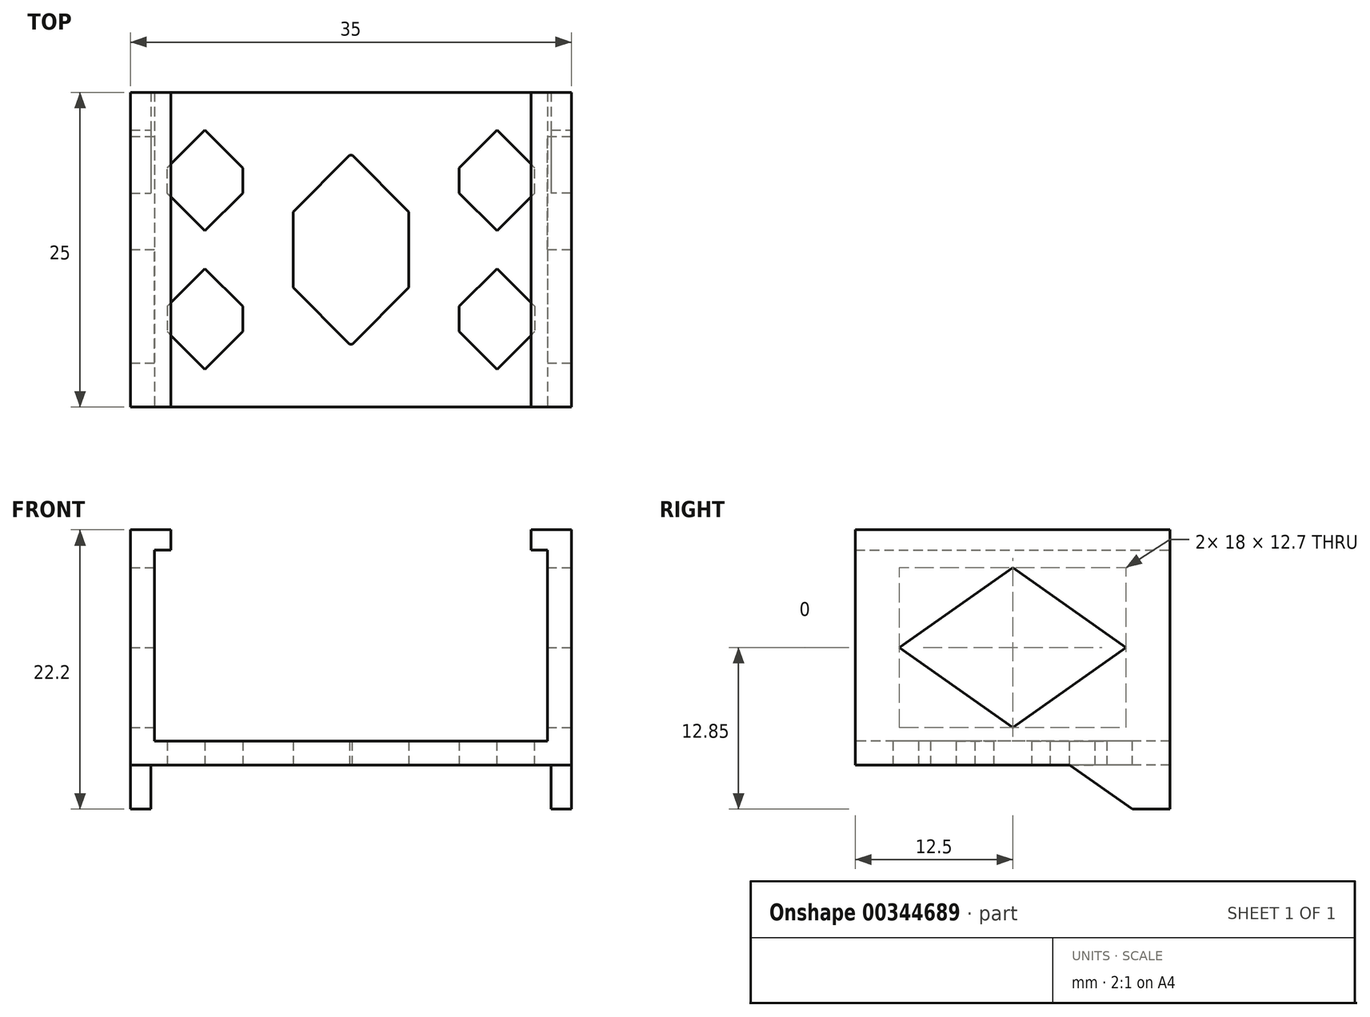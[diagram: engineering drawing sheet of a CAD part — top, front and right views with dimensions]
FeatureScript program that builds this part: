
annotation { "Feature Type Name" : "Feature", "Feature Type Description" : "" }
export const myFeature = defineFeature(function(context is Context, id is Id, definition is map)
    precondition{}
    {
        {
            var Q0;
            Q0=qCreatedBy(makeId("Top.planeOp"),FACE);
            var sketch = newSketch(context, id + "F0", { "sketchPlane" : qUnion([Q0])});
            skLineSegment(sketch, "E0.bottom", {"start": v(-17.5, 15) * mm, "end": v(17.5, 15) * mm});
            skLineSegment(sketch, "E0.top", {"start": v(-17.5, -15) * mm, "end": v(17.5, -15) * mm});
            skLineSegment(sketch, "E0.left", {"start": v(-17.5, 15) * mm, "end": v(-17.5, -15) * mm});
            skLineSegment(sketch, "E0.right", {"start": v(17.5, 15) * mm, "end": v(17.5, -15) * mm});
            skPoint(sketch, "E0.middle", {"position": v(0, 0) * mm});
            skSolve(sketch);
        }
        {
            var Q0;
            Q0=makeQuery(id+"F0.imprint","IMPRINT",FACE,{"disambiguationData":[TD([[makeQuery(id+"F0.imprint","IMPRINT",EDGE,{"derivedFrom":sQuery(id+"F0.wireOp",EDGE,"E0.bottom")}),-1.0]])]});
            extrude(context, id + "F1", {"entities" : qUnion([Q0]), "depth" : 1.9 * mm});
        }
        {
            var Q0;
            {var subQ5=sQuery(id+"F0.wireOp",EDGE,"E0.right");var subQ6=sQuery(id+"F0.wireOp",EDGE,"E0.left");var subQ7=sQuery(id+"F0.wireOp",EDGE,"E0.top");var subQ8=sQuery(id+"F0.wireOp",EDGE,"E0.bottom");var subQ9=makeQuery(id+"F1.opExtrude","CAP_FACE",FACE,{"disambiguationData":[OSD([subQ8,subQ7,subQ6,subQ5])],"isStart":false});var subQ12=subQ9;Q0=makeQuery(id+"FTskU3KK5imesQs_1.opFillet","MERGE",FACE,{"derivedFrom":[makeQuery(id+"FZi3CJKkktuihJ1_1.boolean.opBoolean","SPLIT",FACE,{"disambiguationData":[TD([makeQuery(id+"F1.opExtrude","SWEPT_FACE",FACE,{"disambiguationData":[OSD([subQ8])]})])],"derivedFrom":subQ12}),makeQuery(id+"FZ7EBSF1tdb4njM_1.boolean.opBoolean","MERGE",FACE,{"derivedFrom":[makeQuery(id+"FZi3CJKkktuihJ1_1.boolean.opBoolean","SPLIT",FACE,{"disambiguationData":[TD([makeQuery(id+"FlsG0jWeIkAughT_1.opExtrude","SWEPT_FACE",FACE,{"disambiguationData":[OSD([sQuery(id+"F5Wyuop6bpOGen8_1.wireOp",EDGE,"vaNtV44L-idVL-UOBQ-HHhe-vYpkaX2QMto8.bottom")])]})])],"derivedFrom":subQ12}),makeQuery(id+"FZ7EBSF1tdb4njM_1.opExtrude","CAP_FACE",FACE,{"disambiguationData":[OSD([sQuery(id+"FoSm93bD1NxVTFu_1.wireOp",EDGE,"97a7e462-43fe-4127-a601-1d90c2ab95a00.MirrorCS"),sQuery(id+"FoSm93bD1NxVTFu_1.wireOp",EDGE,"97a7e462-43fe-4127-a601-1d90c2ab95a01.MirrorCS"),sQuery(id+"FoSm93bD1NxVTFu_1.wireOp",EDGE,"97a7e462-43fe-4127-a601-1d90c2ab95a02.MirrorCS"),sQuery(id+"FoSm93bD1NxVTFu_1.wireOp",EDGE,"97a7e462-43fe-4127-a601-1d90c2ab95a03.MirrorCS")])],"isStart":false})]}),makeQuery(id+"FZ7EBSF1tdb4njM_1.boolean.opBoolean","MERGE",FACE,{"derivedFrom":[makeQuery(id+"FZi3CJKkktuihJ1_1.boolean.opBoolean","SPLIT",FACE,{"disambiguationData":[TD([makeQuery(id+"FlsG0jWeIkAughT_1.opExtrude","SWEPT_FACE",FACE,{"disambiguationData":[OSD([sQuery(id+"F5Wyuop6bpOGen8_1.wireOp",EDGE,"5b2c8ccd-c1e1-48dd-aecc-73c440124aab0.MirrorCS")])]})])],"derivedFrom":subQ12}),makeQuery(id+"FZ7EBSF1tdb4njM_1.opExtrude","CAP_FACE",FACE,{"disambiguationData":[OSD([sQuery(id+"FoSm93bD1NxVTFu_1.wireOp",EDGE,"85c03d27-702a-4580-8be8-e1d3315b53173.MirrorCS"),sQuery(id+"FoSm93bD1NxVTFu_1.wireOp",EDGE,"85c03d27-702a-4580-8be8-e1d3315b53174.MirrorCS"),sQuery(id+"FoSm93bD1NxVTFu_1.wireOp",EDGE,"85c03d27-702a-4580-8be8-e1d3315b53176.MirrorCS"),sQuery(id+"FoSm93bD1NxVTFu_1.wireOp",EDGE,"85c03d27-702a-4580-8be8-e1d3315b53177.MirrorCS")])],"isStart":false})]})]});}
            var sketch = newSketch(context, id + "F2", { "sketchPlane" : qUnion([Q0])});
            skLineSegment(sketch, "E1.bottom", {"start": v(-15.6, 14) * mm, "end": v(15.6, 14) * mm});
            skLineSegment(sketch, "E1.top", {"start": v(-15.6, -14) * mm, "end": v(15.6, -14) * mm});
            skLineSegment(sketch, "E1.left", {"start": v(-15.6, 14) * mm, "end": v(-15.6, -14) * mm});
            skLineSegment(sketch, "E1.right", {"start": v(15.6, 14) * mm, "end": v(15.6, -14) * mm});
            skPoint(sketch, "E1.middle", {"position": v(0, 0) * mm});
            skSolve(sketch);
        }
        {
            var Q0;
            Q0=makeQuery(id+"F2.imprint","IMPRINT",FACE,{"disambiguationData":[TD([[makeQuery(id+"F2.imprint","IMPRINT",EDGE,{"derivedFrom":sQuery(id+"F2.wireOp",EDGE,"E1.bottom")}),1.0]])]});
            extrude(context, id + "F3", {"entities" : qUnion([Q0]), "operationType" : NewBodyOperationType.ADD, "depth" : 16.8 * mm});
        }
        {
            var Q0;
            Q0=makeQuery(id+"F3.opExtrude","CAP_FACE",FACE,{"disambiguationData":[OSD([sQuery(id+"F0.wireOp",EDGE,"E0.bottom"),sQuery(id+"F0.wireOp",EDGE,"E0.top"),sQuery(id+"F0.wireOp",EDGE,"E0.left"),sQuery(id+"F0.wireOp",EDGE,"E0.right"),sQuery(id+"F2.wireOp",EDGE,"E1.bottom"),sQuery(id+"F2.wireOp",EDGE,"E1.top"),sQuery(id+"F2.wireOp",EDGE,"E1.left"),sQuery(id+"F2.wireOp",EDGE,"E1.right")])],"isStart":false});
            var sketch = newSketch(context, id + "F4", { "sketchPlane" : qUnion([Q0])});
            skLineSegment(sketch, "E2.bottom", {"start": v(-17.5, -15) * mm, "end": v(17.5, -15) * mm});
            skLineSegment(sketch, "E2.top", {"start": v(-17.5, -12.5) * mm, "end": v(17.5, -12.5) * mm});
            skLineSegment(sketch, "E2.left", {"start": v(-17.5, -15) * mm, "end": v(-17.5, -12.5) * mm});
            skLineSegment(sketch, "E2.right", {"start": v(17.5, -15) * mm, "end": v(17.5, -12.5) * mm});
            skLineSegment(sketch, "E3.MirrorCS", {"start": v(17.5, 15) * mm, "end": v(17.5, 12.5) * mm});
            skLineSegment(sketch, "E4.MirrorCS", {"start": v(-17.5, 15) * mm, "end": v(-17.5, 12.5) * mm});
            skLineSegment(sketch, "E5.MirrorCS", {"start": v(-17.5, 15) * mm, "end": v(17.5, 15) * mm});
            skLineSegment(sketch, "E6.MirrorCS", {"start": v(-17.5, 12.5) * mm, "end": v(17.5, 12.5) * mm});
            skSolve(sketch);
        }
        {
            var Q0;
            Q0=qSketchRegion(id+"F4",true);
            extrude(context, id + "F5", {"entities" : qUnion([Q0]), "operationType" : NewBodyOperationType.REMOVE, "endBound" : BoundingType.THROUGH_ALL, "oppositeDirection" : true, "depth" : 25 * mm});
        }
        {
            var Q0;
            {var subQ5=sQuery(id+"F0.wireOp",EDGE,"E0.right");var subQ6=sQuery(id+"F0.wireOp",EDGE,"E0.left");var subQ7=sQuery(id+"F0.wireOp",EDGE,"E0.top");var subQ8=sQuery(id+"F0.wireOp",EDGE,"E0.bottom");var subQ9=makeQuery(id+"F1.opExtrude","CAP_FACE",FACE,{"disambiguationData":[OSD([subQ8,subQ7,subQ6,subQ5])],"isStart":false});var subQ12=subQ9;Q0=makeQuery(id+"FTskU3KK5imesQs_1.opFillet","MERGE",FACE,{"derivedFrom":[makeQuery(id+"FZi3CJKkktuihJ1_1.boolean.opBoolean","SPLIT",FACE,{"disambiguationData":[TD([makeQuery(id+"F1.opExtrude","SWEPT_FACE",FACE,{"disambiguationData":[OSD([subQ8])]})])],"derivedFrom":subQ12}),makeQuery(id+"FZ7EBSF1tdb4njM_1.boolean.opBoolean","MERGE",FACE,{"derivedFrom":[makeQuery(id+"FZi3CJKkktuihJ1_1.boolean.opBoolean","SPLIT",FACE,{"disambiguationData":[TD([makeQuery(id+"FlsG0jWeIkAughT_1.opExtrude","SWEPT_FACE",FACE,{"disambiguationData":[OSD([sQuery(id+"F5Wyuop6bpOGen8_1.wireOp",EDGE,"vaNtV44L-idVL-UOBQ-HHhe-vYpkaX2QMto8.bottom")])]})])],"derivedFrom":subQ12}),makeQuery(id+"FZ7EBSF1tdb4njM_1.opExtrude","CAP_FACE",FACE,{"disambiguationData":[OSD([sQuery(id+"FoSm93bD1NxVTFu_1.wireOp",EDGE,"97a7e462-43fe-4127-a601-1d90c2ab95a00.MirrorCS"),sQuery(id+"FoSm93bD1NxVTFu_1.wireOp",EDGE,"97a7e462-43fe-4127-a601-1d90c2ab95a01.MirrorCS"),sQuery(id+"FoSm93bD1NxVTFu_1.wireOp",EDGE,"97a7e462-43fe-4127-a601-1d90c2ab95a02.MirrorCS"),sQuery(id+"FoSm93bD1NxVTFu_1.wireOp",EDGE,"97a7e462-43fe-4127-a601-1d90c2ab95a03.MirrorCS")])],"isStart":false})]}),makeQuery(id+"FZ7EBSF1tdb4njM_1.boolean.opBoolean","MERGE",FACE,{"derivedFrom":[makeQuery(id+"FZi3CJKkktuihJ1_1.boolean.opBoolean","SPLIT",FACE,{"disambiguationData":[TD([makeQuery(id+"FlsG0jWeIkAughT_1.opExtrude","SWEPT_FACE",FACE,{"disambiguationData":[OSD([sQuery(id+"F5Wyuop6bpOGen8_1.wireOp",EDGE,"5b2c8ccd-c1e1-48dd-aecc-73c440124aab0.MirrorCS")])]})])],"derivedFrom":subQ12}),makeQuery(id+"FZ7EBSF1tdb4njM_1.opExtrude","CAP_FACE",FACE,{"disambiguationData":[OSD([sQuery(id+"FoSm93bD1NxVTFu_1.wireOp",EDGE,"85c03d27-702a-4580-8be8-e1d3315b53173.MirrorCS"),sQuery(id+"FoSm93bD1NxVTFu_1.wireOp",EDGE,"85c03d27-702a-4580-8be8-e1d3315b53174.MirrorCS"),sQuery(id+"FoSm93bD1NxVTFu_1.wireOp",EDGE,"85c03d27-702a-4580-8be8-e1d3315b53176.MirrorCS"),sQuery(id+"FoSm93bD1NxVTFu_1.wireOp",EDGE,"85c03d27-702a-4580-8be8-e1d3315b53177.MirrorCS")])],"isStart":false})]})]});}
            var sketch = newSketch(context, id + "F6", { "sketchPlane" : qUnion([Q0])});
            skLineSegment(sketch, "E7.bottom", {"start": v(-15.6, -5.25) * mm, "end": v(-13.6, -5.25) * mm});
            skLineSegment(sketch, "E7.top", {"start": v(-15.6, 5.25) * mm, "end": v(-13.6, 5.25) * mm});
            skLineSegment(sketch, "E7.left", {"start": v(-15.6, -5.25) * mm, "end": v(-15.6, 5.25) * mm});
            skLineSegment(sketch, "E7.right", {"start": v(15.6, -5.25) * mm, "end": v(15.6, 5.25) * mm});
            skLineSegment(sketch, "E8.bottom", {"start": v(-15.6, -7.25) * mm, "end": v(-13.6, -7.25) * mm});
            skLineSegment(sketch, "E8.top", {"start": v(-15.6, -12.5) * mm, "end": v(-13.6, -12.5) * mm});
            skLineSegment(sketch, "E8.left", {"start": v(-15.6, -7.25) * mm, "end": v(-15.6, -12.5) * mm});
            skLineSegment(sketch, "E8.right", {"start": v(15.6, -7.25) * mm, "end": v(15.6, -12.5) * mm});
            skLineSegment(sketch, "E9.MirrorCS", {"start": v(-15.6, 7.25) * mm, "end": v(-13.6, 7.25) * mm});
            skLineSegment(sketch, "E10.MirrorCS", {"start": v(-15.6, 12.5) * mm, "end": v(15.6, 12.5) * mm});
            skLineSegment(sketch, "E11.MirrorCS", {"start": v(15.6, 7.25) * mm, "end": v(15.6, 12.5) * mm});
            skLineSegment(sketch, "E12.MirrorCS", {"start": v(-15.6, 7.25) * mm, "end": v(-15.6, 12.5) * mm});
            skLineSegment(sketch, "E13", {"start": v(-13.6, -12.5) * mm, "end": v(-13.6, -7.25) * mm});
            skLineSegment(sketch, "E14.MirrorCS", {"start": v(13.6, -12.5) * mm, "end": v(13.6, -7.25) * mm});
            skLineSegment(sketch, "E15.trimOffspring", {"start": v(-13.6, -5.25) * mm, "end": v(-13.6, 5.25) * mm});
            skLineSegment(sketch, "E16.trimOffspring", {"start": v(13.6, -7.25) * mm, "end": v(15.6, -7.25) * mm});
            skLineSegment(sketch, "E17.trimOffspring", {"start": v(13.6, -12.5) * mm, "end": v(15.6, -12.5) * mm});
            skLineSegment(sketch, "E18.trimOffspring", {"start": v(13.6, -5.25) * mm, "end": v(15.6, -5.25) * mm});
            skLineSegment(sketch, "E19.trimOffspring", {"start": v(13.6, 5.25) * mm, "end": v(15.6, 5.25) * mm});
            skLineSegment(sketch, "E20.trimOffspring", {"start": v(13.6, 7.25) * mm, "end": v(15.6, 7.25) * mm});
            skLineSegment(sketch, "E21.trimOffspring", {"start": v(-13.6, 7.25) * mm, "end": v(-13.6, 12.5) * mm});
            skLineSegment(sketch, "E22.trimOffspring", {"start": v(13.6, -5.25) * mm, "end": v(13.6, 5.25) * mm});
            skLineSegment(sketch, "E23.trimOffspring", {"start": v(13.6, 7.25) * mm, "end": v(13.6, 12.5) * mm});
            skSolve(sketch);
        }
        {
            var Q0;
            Q0=makeQuery(id+"F6.imprint","IMPRINT",FACE,{"disambiguationData":[TD([[makeQuery(id+"F6.imprint","IMPRINT",EDGE,{"derivedFrom":sQuery(id+"F6.wireOp",EDGE,"E8.bottom")}),-1.0]])]});
            var Q1;
            Q1=makeQuery(id+"F6.imprint","IMPRINT",FACE,{"disambiguationData":[TD([[makeQuery(id+"F6.imprint","IMPRINT",EDGE,{"derivedFrom":sQuery(id+"F6.wireOp",EDGE,"E7.bottom")}),1.0]])]});
            var Q2;
            Q2=makeQuery(id+"F6.imprint","IMPRINT",FACE,{"disambiguationData":[TD([[makeQuery(id+"F6.imprint","IMPRINT",EDGE,{"derivedFrom":sQuery(id+"F6.wireOp",EDGE,"E9.MirrorCS")}),1.0]])]});
            var Q3;
            Q3=makeQuery(id+"F6.imprint","IMPRINT",FACE,{"disambiguationData":[TD([[makeQuery(id+"F6.imprint","IMPRINT",EDGE,{"derivedFrom":sQuery(id+"F6.wireOp",EDGE,"E8.right")}),-1.0]])]});
            var Q4;
            Q4=makeQuery(id+"F6.imprint","IMPRINT",FACE,{"disambiguationData":[TD([[makeQuery(id+"F6.imprint","IMPRINT",EDGE,{"derivedFrom":sQuery(id+"F6.wireOp",EDGE,"E7.right")}),-1.0]])]});
            var Q5;
            {var subQ0=sQuery(id+"F6.wireOp",EDGE,"E11.MirrorCS");Q5=makeQuery(id+"F6.imprint","IMPRINT",FACE,{"disambiguationData":[TD([[makeQuery(id+"F6.imprint","IMPRINT",EDGE,{"derivedFrom":subQ0}),-1.0]])]});}
            extrude(context, id + "F7", {"entities" : qUnion([Q0, Q1, Q2, Q3, Q4, Q5]), "operationType" : NewBodyOperationType.REMOVE, "depth" : 30 * mm});
        }
        {
            var Q0;
            Q0=makeQuery(id+"F5.boolean.opBoolean","COPY",FACE,{"derivedFrom":makeQuery(id+"F5.opExtrude","SWEPT_FACE",FACE,{"disambiguationData":[OSD([sQuery(id+"F4.wireOp",EDGE,"E6.MirrorCS")])]})});
            var sketch = newSketch(context, id + "F8", { "sketchPlane" : qUnion([Q0])});
            skLineSegment(sketch, "E24", {"start": v(-15.6, 18.7) * mm, "end": v(-14.3, 18.7) * mm});
            skLineSegment(sketch, "E25", {"start": v(-15.6, 17.1) * mm, "end": v(-15.6, 18.7) * mm});
            skLineSegment(sketch, "E26", {"start": v(-15.6, 17.1) * mm, "end": v(-14.3, 17.1) * mm});
            skLineSegment(sketch, "E27", {"start": v(-14.3, 17.1) * mm, "end": v(-14.3, 18.7) * mm});
            skLineSegment(sketch, "E28.MirrorCS", {"start": v(15.6, 18.7) * mm, "end": v(14.3, 18.7) * mm});
            skLineSegment(sketch, "E29.MirrorCS", {"start": v(15.6, 17.1) * mm, "end": v(14.3, 17.1) * mm});
            skLineSegment(sketch, "E30.MirrorCS", {"start": v(15.6, 17.1) * mm, "end": v(15.6, 18.7) * mm});
            skLineSegment(sketch, "E31.MirrorCS", {"start": v(14.3, 17.1) * mm, "end": v(14.3, 18.7) * mm});
            skSolve(sketch);
        }
        {
            var Q0;
            Q0=makeQuery(id+"F8.imprint","IMPRINT",FACE,{"disambiguationData":[TD([[makeQuery(id+"F8.imprint","IMPRINT",EDGE,{"derivedFrom":sQuery(id+"F8.wireOp",EDGE,"E24")}),-1.0]])]});
            var Q1;
            Q1=makeQuery(id+"F8.imprint","IMPRINT",FACE,{"disambiguationData":[TD([[makeQuery(id+"F8.imprint","IMPRINT",EDGE,{"derivedFrom":sQuery(id+"F8.wireOp",EDGE,"E28.MirrorCS")}),1.0]])]});
            var Q2;
            Q2=makeQuery(id+"F5.boolean.opBoolean","COPY",FACE,{"derivedFrom":makeQuery(id+"F5.opExtrude","SWEPT_FACE",FACE,{"disambiguationData":[OSD([sQuery(id+"F4.wireOp",EDGE,"E2.top")])]})});
            extrude(context, id + "F9", {"entities" : qUnion([Q0, Q1]), "operationType" : NewBodyOperationType.ADD, "endBound" : BoundingType.UP_TO_SURFACE, "oppositeDirection" : true, "endBoundEntityFace" : qUnion([Q2]), "depth" : 25 * mm});
        }
        {
            var Q0;
            Q0=makeQuery(id+"F1.opExtrude","CAP_FACE",FACE,{"disambiguationData":[OSD([sQuery(id+"F0.wireOp",EDGE,"E0.bottom"),sQuery(id+"F0.wireOp",EDGE,"E0.top"),sQuery(id+"F0.wireOp",EDGE,"E0.left"),sQuery(id+"F0.wireOp",EDGE,"E0.right")])],"isStart":false});
            var sketch = newSketch(context, id + "F10", { "sketchPlane" : qUnion([Q0])});
            skLineSegment(sketch, "E32.bottom", {"start": v(-8.6, 1.5) * mm, "end": v(-14.6, 1.5) * mm});
            skLineSegment(sketch, "E32.top", {"start": v(-8.6, 9.5) * mm, "end": v(-14.6, 9.5) * mm});
            skLineSegment(sketch, "E32.left", {"start": v(-8.6, 1.5) * mm, "end": v(-8.6, 9.5) * mm});
            skLineSegment(sketch, "E32.right", {"start": v(-14.6, 1.5) * mm, "end": v(-14.6, 9.5) * mm});
            skPoint(sketch, "E32.middle", {"position": v(-11.6, 5.5) * mm});
            skLineSegment(sketch, "E33.MirrorCS", {"start": v(-8.6, -9.5) * mm, "end": v(-14.6, -9.5) * mm});
            skLineSegment(sketch, "E34.MirrorCS", {"start": v(-8.6, -1.5) * mm, "end": v(-14.6, -1.5) * mm});
            skLineSegment(sketch, "E35.MirrorCS", {"start": v(-8.6, -1.5) * mm, "end": v(-8.6, -9.5) * mm});
            skLineSegment(sketch, "E36.MirrorCS", {"start": v(-14.6, -1.5) * mm, "end": v(-14.6, -9.5) * mm});
            skPoint(sketch, "E37.MirrorP", {"position": v(-11.6, -5.5) * mm});
            skLineSegment(sketch, "E38.MirrorCS", {"start": v(8.6, -1.5) * mm, "end": v(14.6, -1.5) * mm});
            skPoint(sketch, "E39.MirrorP", {"position": v(11.6, 5.5) * mm});
            skLineSegment(sketch, "E40.MirrorCS", {"start": v(8.6, -9.5) * mm, "end": v(14.6, -9.5) * mm});
            skLineSegment(sketch, "E41.MirrorCS", {"start": v(8.6, 1.5) * mm, "end": v(14.6, 1.5) * mm});
            skLineSegment(sketch, "E42.MirrorCS", {"start": v(8.6, 9.5) * mm, "end": v(14.6, 9.5) * mm});
            skLineSegment(sketch, "E43.MirrorCS", {"start": v(14.6, -1.5) * mm, "end": v(14.6, -9.5) * mm});
            skLineSegment(sketch, "E44.MirrorCS", {"start": v(8.6, -1.5) * mm, "end": v(8.6, -9.5) * mm});
            skLineSegment(sketch, "E45.MirrorCS", {"start": v(14.6, 1.5) * mm, "end": v(14.6, 9.5) * mm});
            skLineSegment(sketch, "E46.MirrorCS", {"start": v(8.6, 1.5) * mm, "end": v(8.6, 9.5) * mm});
            skPoint(sketch, "E47.MirrorP", {"position": v(11.6, -5.5) * mm});
            skLineSegment(sketch, "E48.bottom", {"start": v(-4.6, 7.5) * mm, "end": v(4.6, 7.5) * mm});
            skLineSegment(sketch, "E48.top", {"start": v(-4.6, -7.5) * mm, "end": v(4.6, -7.5) * mm});
            skLineSegment(sketch, "E48.left", {"start": v(-4.6, 7.5) * mm, "end": v(-4.6, -7.5) * mm});
            skLineSegment(sketch, "E48.right", {"start": v(4.6, 7.5) * mm, "end": v(4.6, -7.5) * mm});
            skPoint(sketch, "E48.middle", {"position": v(0, 0) * mm});
            skSolve(sketch);
        }
        {
            var Q0;
            Q0=makeQuery(id+"F10.imprint","IMPRINT",FACE,{"disambiguationData":[TD([[makeQuery(id+"F10.imprint","IMPRINT",EDGE,{"derivedFrom":sQuery(id+"F10.wireOp",EDGE,"E32.bottom")}),-1.0]])]});
            var Q1;
            Q1=makeQuery(id+"F10.imprint","IMPRINT",FACE,{"disambiguationData":[TD([[makeQuery(id+"F10.imprint","IMPRINT",EDGE,{"derivedFrom":sQuery(id+"F10.wireOp",EDGE,"E33.MirrorCS")}),-1.0]])]});
            var Q2;
            Q2=makeQuery(id+"F10.imprint","IMPRINT",FACE,{"disambiguationData":[TD([[makeQuery(id+"F10.imprint","IMPRINT",EDGE,{"derivedFrom":sQuery(id+"F10.wireOp",EDGE,"E41.MirrorCS")}),1.0]])]});
            var Q3;
            Q3=makeQuery(id+"F10.imprint","IMPRINT",FACE,{"disambiguationData":[TD([[makeQuery(id+"F10.imprint","IMPRINT",EDGE,{"derivedFrom":sQuery(id+"F10.wireOp",EDGE,"E38.MirrorCS")}),-1.0]])]});
            var Q4;
            Q4=makeQuery(id+"F10.imprint","IMPRINT",FACE,{"disambiguationData":[TD([[makeQuery(id+"F10.imprint","IMPRINT",EDGE,{"derivedFrom":sQuery(id+"F10.wireOp",EDGE,"E48.bottom")}),-1.0]])]});
            extrude(context, id + "F11", {"entities" : qUnion([Q0, Q1, Q2, Q3, Q4]), "operationType" : NewBodyOperationType.REMOVE, "oppositeDirection" : true, "depth" : 25 * mm});
        }
        {
            var Q0;
            Q0=makeQuery(id+"F11.boolean.opBoolean","COPY",EDGE,{"derivedFrom":makeQuery(id+"F11.opExtrude","SWEPT_EDGE",EDGE,{"disambiguationData":[OSD([sQuery(id+"F10.wireOp",EDGE,"E40.MirrorCS"),sQuery(id+"F10.wireOp",EDGE,"E43.MirrorCS")])]})});
            var Q1;
            Q1=makeQuery(id+"F11.boolean.opBoolean","COPY",EDGE,{"derivedFrom":makeQuery(id+"F11.opExtrude","SWEPT_EDGE",EDGE,{"disambiguationData":[OSD([sQuery(id+"F10.wireOp",EDGE,"E40.MirrorCS"),sQuery(id+"F10.wireOp",EDGE,"E44.MirrorCS")])]})});
            var Q2;
            Q2=makeQuery(id+"F11.boolean.opBoolean","COPY",EDGE,{"derivedFrom":makeQuery(id+"F11.opExtrude","SWEPT_EDGE",EDGE,{"disambiguationData":[OSD([sQuery(id+"F10.wireOp",EDGE,"E38.MirrorCS"),sQuery(id+"F10.wireOp",EDGE,"E44.MirrorCS")])]})});
            var Q3;
            Q3=makeQuery(id+"F11.boolean.opBoolean","COPY",EDGE,{"derivedFrom":makeQuery(id+"F11.opExtrude","SWEPT_EDGE",EDGE,{"disambiguationData":[OSD([sQuery(id+"F10.wireOp",EDGE,"E38.MirrorCS"),sQuery(id+"F10.wireOp",EDGE,"E43.MirrorCS")])]})});
            var Q4;
            Q4=makeQuery(id+"F11.boolean.opBoolean","COPY",EDGE,{"derivedFrom":makeQuery(id+"F11.opExtrude","SWEPT_EDGE",EDGE,{"disambiguationData":[OSD([sQuery(id+"F10.wireOp",EDGE,"E42.MirrorCS"),sQuery(id+"F10.wireOp",EDGE,"E45.MirrorCS")])]})});
            var Q5;
            Q5=makeQuery(id+"F11.boolean.opBoolean","COPY",EDGE,{"derivedFrom":makeQuery(id+"F11.opExtrude","SWEPT_EDGE",EDGE,{"disambiguationData":[OSD([sQuery(id+"F10.wireOp",EDGE,"E32.top"),sQuery(id+"F10.wireOp",EDGE,"E32.left")])]})});
            var Q6;
            Q6=makeQuery(id+"F11.boolean.opBoolean","COPY",EDGE,{"derivedFrom":makeQuery(id+"F11.opExtrude","SWEPT_EDGE",EDGE,{"disambiguationData":[OSD([sQuery(id+"F10.wireOp",EDGE,"E34.MirrorCS"),sQuery(id+"F10.wireOp",EDGE,"E35.MirrorCS")])]})});
            var Q7;
            Q7=makeQuery(id+"F11.boolean.opBoolean","COPY",EDGE,{"derivedFrom":makeQuery(id+"F11.opExtrude","SWEPT_EDGE",EDGE,{"disambiguationData":[OSD([sQuery(id+"F10.wireOp",EDGE,"E41.MirrorCS"),sQuery(id+"F10.wireOp",EDGE,"E45.MirrorCS")])]})});
            var Q8;
            Q8=makeQuery(id+"F11.boolean.opBoolean","COPY",EDGE,{"derivedFrom":makeQuery(id+"F11.opExtrude","SWEPT_EDGE",EDGE,{"disambiguationData":[OSD([sQuery(id+"F10.wireOp",EDGE,"E33.MirrorCS"),sQuery(id+"F10.wireOp",EDGE,"E35.MirrorCS")])]})});
            var Q9;
            Q9=makeQuery(id+"F11.boolean.opBoolean","COPY",EDGE,{"derivedFrom":makeQuery(id+"F11.opExtrude","SWEPT_EDGE",EDGE,{"disambiguationData":[OSD([sQuery(id+"F10.wireOp",EDGE,"E32.bottom"),sQuery(id+"F10.wireOp",EDGE,"E32.left")])]})});
            var Q10;
            Q10=makeQuery(id+"F11.boolean.opBoolean","COPY",EDGE,{"derivedFrom":makeQuery(id+"F11.opExtrude","SWEPT_EDGE",EDGE,{"disambiguationData":[OSD([sQuery(id+"F10.wireOp",EDGE,"E34.MirrorCS"),sQuery(id+"F10.wireOp",EDGE,"E36.MirrorCS")])]})});
            var Q11;
            Q11=makeQuery(id+"F11.boolean.opBoolean","COPY",EDGE,{"derivedFrom":makeQuery(id+"F11.opExtrude","SWEPT_EDGE",EDGE,{"disambiguationData":[OSD([sQuery(id+"F10.wireOp",EDGE,"E32.top"),sQuery(id+"F10.wireOp",EDGE,"E32.right")])]})});
            var Q12;
            Q12=makeQuery(id+"F11.boolean.opBoolean","COPY",EDGE,{"derivedFrom":makeQuery(id+"F11.opExtrude","SWEPT_EDGE",EDGE,{"disambiguationData":[OSD([sQuery(id+"F10.wireOp",EDGE,"E42.MirrorCS"),sQuery(id+"F10.wireOp",EDGE,"E46.MirrorCS")])]})});
            var Q13;
            Q13=makeQuery(id+"F11.boolean.opBoolean","COPY",EDGE,{"derivedFrom":makeQuery(id+"F11.opExtrude","SWEPT_EDGE",EDGE,{"disambiguationData":[OSD([sQuery(id+"F10.wireOp",EDGE,"E41.MirrorCS"),sQuery(id+"F10.wireOp",EDGE,"E46.MirrorCS")])]})});
            var Q14;
            Q14=makeQuery(id+"F11.boolean.opBoolean","COPY",EDGE,{"derivedFrom":makeQuery(id+"F11.opExtrude","SWEPT_EDGE",EDGE,{"disambiguationData":[OSD([sQuery(id+"F10.wireOp",EDGE,"E32.bottom"),sQuery(id+"F10.wireOp",EDGE,"E32.right")])]})});
            var Q15;
            Q15=makeQuery(id+"F11.boolean.opBoolean","COPY",EDGE,{"derivedFrom":makeQuery(id+"F11.opExtrude","SWEPT_EDGE",EDGE,{"disambiguationData":[OSD([sQuery(id+"F10.wireOp",EDGE,"E33.MirrorCS"),sQuery(id+"F10.wireOp",EDGE,"E36.MirrorCS")])]})});
            chamfer(context, id + "F12", {"entities" : qUnion([Q0, Q1, Q2, Q3, Q4, Q5, Q6, Q7, Q8, Q9, Q10, Q11, Q12, Q13, Q14, Q15]), "width" : 3 * mm, "tangentPropagation" : true});
        }
        {
            var Q0;
            Q0=makeQuery(id+"F11.boolean.opBoolean","COPY",EDGE,{"derivedFrom":makeQuery(id+"F11.opExtrude","SWEPT_EDGE",EDGE,{"disambiguationData":[OSD([sQuery(id+"F10.wireOp",EDGE,"E48.top"),sQuery(id+"F10.wireOp",EDGE,"E48.right")])]})});
            var Q1;
            Q1=makeQuery(id+"F11.boolean.opBoolean","COPY",EDGE,{"derivedFrom":makeQuery(id+"F11.opExtrude","SWEPT_EDGE",EDGE,{"disambiguationData":[OSD([sQuery(id+"F10.wireOp",EDGE,"E48.top"),sQuery(id+"F10.wireOp",EDGE,"E48.left")])]})});
            var Q2;
            Q2=makeQuery(id+"F11.boolean.opBoolean","COPY",EDGE,{"derivedFrom":makeQuery(id+"F11.opExtrude","SWEPT_EDGE",EDGE,{"disambiguationData":[OSD([sQuery(id+"F10.wireOp",EDGE,"E48.bottom"),sQuery(id+"F10.wireOp",EDGE,"E48.right")])]})});
            var Q3;
            Q3=makeQuery(id+"F11.boolean.opBoolean","COPY",EDGE,{"derivedFrom":makeQuery(id+"F11.opExtrude","SWEPT_EDGE",EDGE,{"disambiguationData":[OSD([sQuery(id+"F10.wireOp",EDGE,"E48.bottom"),sQuery(id+"F10.wireOp",EDGE,"E48.left")])]})});
            chamfer(context, id + "F13", {"entities" : qUnion([Q0, Q1, Q2, Q3]), "width" : 4.5 * mm, "tangentPropagation" : true});
        }
        {
            var Q0;
            Q0=makeQuery(id+"F1.opExtrude","CAP_FACE",FACE,{"disambiguationData":[OSD([sQuery(id+"F0.wireOp",EDGE,"E0.bottom"),sQuery(id+"F0.wireOp",EDGE,"E0.top"),sQuery(id+"F0.wireOp",EDGE,"E0.left"),sQuery(id+"F0.wireOp",EDGE,"E0.right")])],"isStart":true});
            var sketch = newSketch(context, id + "F14", { "sketchPlane" : qUnion([Q0])});
            skLineSegment(sketch, "E49.bottom", {"start": v(17.5, -12.5) * mm, "end": v(15.9, -12.5) * mm});
            skLineSegment(sketch, "E49.top", {"start": v(17.5, -4.5) * mm, "end": v(15.9, -4.5) * mm});
            skLineSegment(sketch, "E49.left", {"start": v(17.5, -12.5) * mm, "end": v(17.5, -4.5) * mm});
            skLineSegment(sketch, "E49.right", {"start": v(15.9, -12.5) * mm, "end": v(15.9, -4.5) * mm});
            skLineSegment(sketch, "E50.MirrorCS", {"start": v(-17.5, -4.5) * mm, "end": v(-15.9, -4.5) * mm});
            skLineSegment(sketch, "E51.MirrorCS", {"start": v(-17.5, -12.5) * mm, "end": v(-15.9, -12.5) * mm});
            skLineSegment(sketch, "E52.MirrorCS", {"start": v(-17.5, -12.5) * mm, "end": v(-17.5, -4.5) * mm});
            skLineSegment(sketch, "E53.MirrorCS", {"start": v(-15.9, -12.5) * mm, "end": v(-15.9, -4.5) * mm});
            skSolve(sketch);
        }
        {
            var Q0;
            Q0=makeQuery(id+"F14.imprint","IMPRINT",FACE,{"disambiguationData":[TD([[makeQuery(id+"F14.imprint","IMPRINT",EDGE,{"derivedFrom":sQuery(id+"F14.wireOp",EDGE,"E49.bottom")}),1.0]])]});
            var Q1;
            Q1=makeQuery(id+"F14.imprint","IMPRINT",FACE,{"disambiguationData":[TD([[makeQuery(id+"F14.imprint","IMPRINT",EDGE,{"derivedFrom":sQuery(id+"F14.wireOp",EDGE,"E50.MirrorCS")}),-1.0]])]});
            extrude(context, id + "F15", {"entities" : qUnion([Q0, Q1]), "operationType" : NewBodyOperationType.ADD, "depth" : 3.5 * mm});
        }
        {
            var Q0;
            {var subQ0=sQuery(id+"F0.wireOp",EDGE,"E0.right");Q0=makeQuery(id+"F15.boolean.opBoolean","MERGE",FACE,{"derivedFrom":[makeQuery(id+"F3.boolean.opBoolean","MERGE",FACE,{"derivedFrom":[makeQuery(id+"F1.opExtrude","SWEPT_FACE",FACE,{"disambiguationData":[OSD([subQ0])]}),makeQuery(id+"F3.opExtrude","SWEPT_FACE",FACE,{"disambiguationData":[OSD([subQ0])]})]}),makeQuery(id+"F15.opExtrude","SWEPT_FACE",FACE,{"disambiguationData":[OSD([sQuery(id+"F14.wireOp",EDGE,"E49.left")])]})]});}
            var sketch = newSketch(context, id + "F16", { "sketchPlane" : qUnion([Q0])});
            skLineSegment(sketch, "E54", {"start": v(0, 15.7) * mm, "end": v(-9, 9.35) * mm});
            skLineSegment(sketch, "E55", {"start": v(-9, 9.35) * mm, "end": v(0, 3) * mm});
            skLineSegment(sketch, "E56", {"start": v(0, 3) * mm, "end": v(9, 9.35) * mm});
            skLineSegment(sketch, "E57", {"start": v(9, 9.35) * mm, "end": v(0, 15.7) * mm});
            skLineSegment(sketch, "E58", {"start": v(-58.52, 9.35) * mm, "end": v(86.8, 9.35) * mm, "construction": true});
            skSolve(sketch);
        }
        {
            var Q0;
            Q0=makeQuery(id+"F16.imprint","IMPRINT",FACE,{"disambiguationData":[TD([[makeQuery(id+"F16.imprint","IMPRINT",EDGE,{"derivedFrom":sQuery(id+"F16.wireOp",EDGE,"E54")}),1.0]])]});
            extrude(context, id + "F17", {"entities" : qUnion([Q0]), "operationType" : NewBodyOperationType.REMOVE, "oppositeDirection" : true, "depth" : 39.3 * mm});
        }
        {
            var Q0;
            {var subQ0=sQuery(id+"F14.wireOp",EDGE,"E49.left");var subQ1=sQuery(id+"F0.wireOp",EDGE,"E0.right");Q0=makeQuery(id+"FFJph5fxpIZx9Oy_1.1.F15.boolean.opBoolean","MERGE",FACE,{"derivedFrom":[makeQuery(id+"F15.boolean.opBoolean","MERGE",FACE,{"derivedFrom":[makeQuery(id+"F3.boolean.opBoolean","MERGE",FACE,{"derivedFrom":[makeQuery(id+"F1.opExtrude","SWEPT_FACE",FACE,{"disambiguationData":[OSD([subQ1])]}),makeQuery(id+"F3.opExtrude","SWEPT_FACE",FACE,{"disambiguationData":[OSD([subQ1])]})]}),makeQuery(id+"F15.opExtrude","SWEPT_FACE",FACE,{"disambiguationData":[OSD([subQ0])]})]}),makeQuery(id+"FFJph5fxpIZx9Oy_1.1.F15.opExtrude","SWEPT_FACE",FACE,{"disambiguationData":[OSD([subQ0])]})]});}
            var sketch = newSketch(context, id + "F18", { "sketchPlane" : qUnion([Q0])});
            skLineSegment(sketch, "E59", {"start": v(4.5, 0) * mm, "end": v(9.5, -3.5) * mm});
            skLineSegment(sketch, "E60", {"start": v(9.5, -3.5) * mm, "end": v(0, -3.5) * mm});
            skLineSegment(sketch, "E61", {"start": v(0, 0) * mm, "end": v(4.5, 0) * mm});
            skLineSegment(sketch, "E62.MirrorCS", {"start": v(-9.5, -3.5) * mm, "end": v(0, -3.5) * mm});
            skLineSegment(sketch, "E63.MirrorCS", {"start": v(-4.5, 0) * mm, "end": v(-9.5, -3.5) * mm});
            skLineSegment(sketch, "E64.MirrorCS", {"start": v(0, 0) * mm, "end": v(-4.5, 0) * mm});
            skSolve(sketch);
        }
        {
            var Q0;
            {var subQ3=sQuery(id+"F18.wireOp",EDGE,"E63.MirrorCS");Q0=makeQuery(id+"F18.imprint","IMPRINT",FACE,{"disambiguationData":[TD([[makeQuery(id+"F18.imprint","IMPRINT",EDGE,{"derivedFrom":subQ3}),1.0]])]});}
            var Q1;
            {var subQ0=sQuery(id+"F18.wireOp",EDGE,"E59");Q1=makeQuery(id+"F18.imprint","IMPRINT",FACE,{"disambiguationData":[TD([[makeQuery(id+"F18.imprint","IMPRINT",EDGE,{"derivedFrom":subQ0}),-1.0]])]});}
            extrude(context, id + "F19", {"entities" : qUnion([Q0, Q1]), "operationType" : NewBodyOperationType.REMOVE, "endBound" : BoundingType.THROUGH_ALL, "oppositeDirection" : true, "depth" : 25 * mm});
        }
    });
